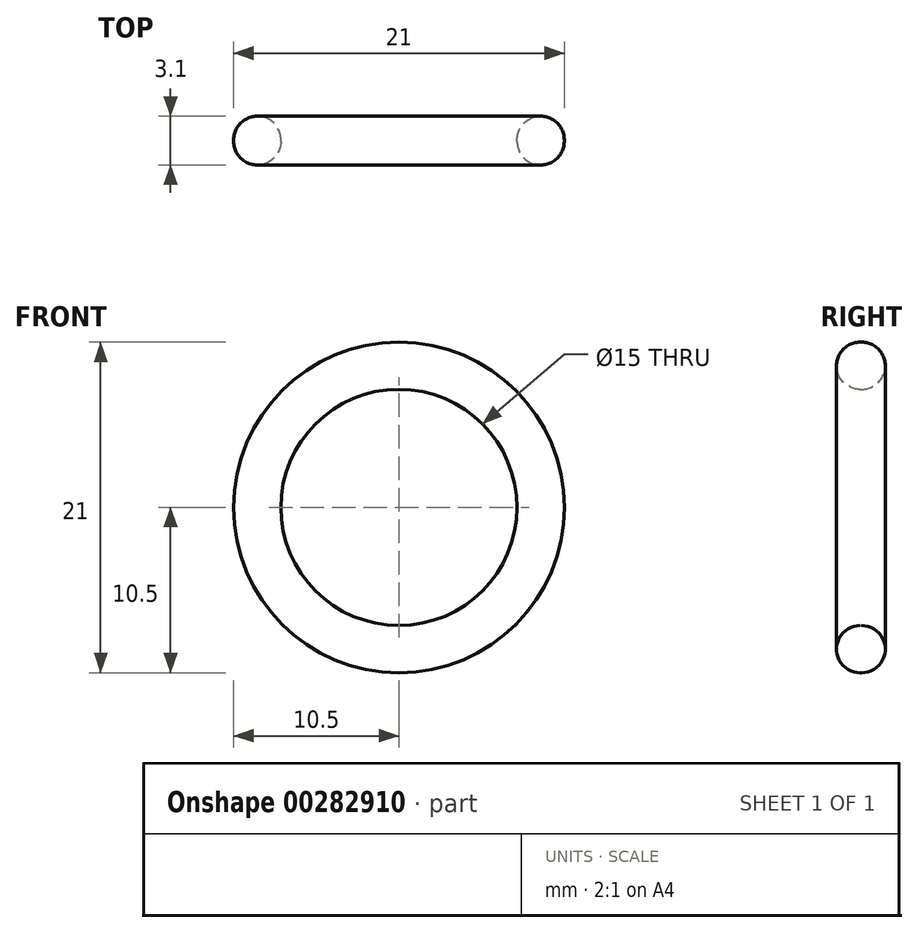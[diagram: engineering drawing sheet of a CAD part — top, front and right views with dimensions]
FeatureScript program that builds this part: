
annotation { "Feature Type Name" : "Feature", "Feature Type Description" : "" }
export const myFeature = defineFeature(function(context is Context, id is Id, definition is map)
    precondition{}
    {
        {
            var Q0;
            Q0=qCreatedBy(makeId("Front.planeOp"),FACE);
            var sketch = newSketch(context, id + "F0", { "sketchPlane" : qUnion([Q0])});
            skCircle(sketch, "E0", {"center": v(0, 0) * mm, "radius": 10.5 * mm});
            skCircle(sketch, "E1", {"center": v(0, 0) * mm, "radius": 7.5 * mm});
            skSolve(sketch);
        }
        {
            var Q0;
            Q0=makeQuery(id+"F0.imprint","IMPRINT",FACE,{"disambiguationData":[TD([[makeQuery(id+"F0.imprint","IMPRINT",EDGE,{"derivedFrom":sQuery(id+"F0.wireOp",EDGE,"E0")}),1.0]])]});
            extrude(context, id + "F1", {"entities" : qUnion([Q0]), "endBound" : BoundingType.SYMMETRIC, "depth" : 3.1 * mm});
        }
        {
            var Q0;
            Q0=makeQuery(id+"F1.opExtrude","CAP_EDGE",EDGE,{"disambiguationData":[OSD([sQuery(id+"F0.wireOp",EDGE,"E0")])],"isStart":false});
            var Q1;
            Q1=makeQuery(id+"F1.opExtrude","CAP_EDGE",EDGE,{"disambiguationData":[OSD([sQuery(id+"F0.wireOp",EDGE,"E0")])],"isStart":true});
            var Q2;
            Q2=makeQuery(id+"F1.opExtrude","CAP_EDGE",EDGE,{"disambiguationData":[OSD([sQuery(id+"F0.wireOp",EDGE,"E1")])],"isStart":true});
            var Q3;
            Q3=makeQuery(id+"F1.opExtrude","CAP_EDGE",EDGE,{"disambiguationData":[OSD([sQuery(id+"F0.wireOp",EDGE,"E1")])],"isStart":false});
            fillet(context, id + "F2", {"entities" : qUnion([Q0, Q1, Q2, Q3]), "radius" : 1.5 * mm, "tangentPropagation" : true, "allowEdgeOverflow" : false});
        }
    });
